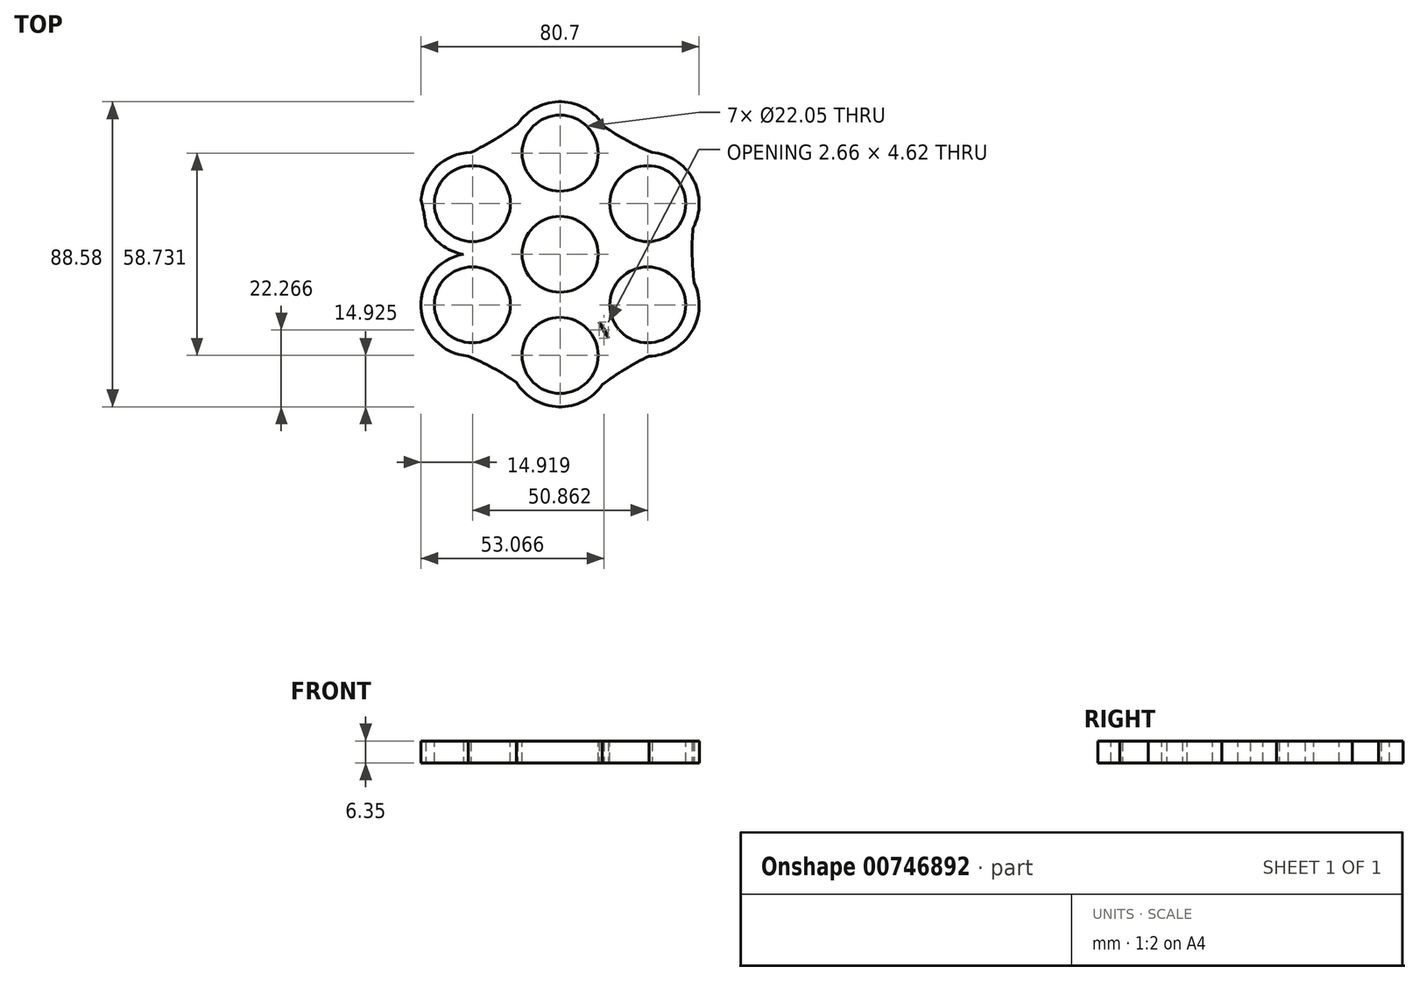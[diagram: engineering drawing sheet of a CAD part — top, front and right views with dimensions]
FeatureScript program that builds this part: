
annotation { "Feature Type Name" : "Feature", "Feature Type Description" : "" }
export const myFeature = defineFeature(function(context is Context, id is Id, definition is map)
    precondition{}
    {
        {
            var Q0;
            Q0=qCreatedBy(makeId("Top.planeOp"),FACE);
            var sketch = newSketch(context, id + "F0", { "sketchPlane" : qUnion([Q0])});
            skCircle(sketch, "E0", {"center": v(0, 0) * mm, "radius": 14.92 * mm});
            skCircle(sketch, "E1", {"center": v(0, 29.37) * mm, "radius": 14.92 * mm});
            skCircle(sketch, "E2.1.0", {"center": v(-25.43, 14.68) * mm, "radius": 14.92 * mm});
            skCircle(sketch, "E2.2.0", {"center": v(-25.43, -14.68) * mm, "radius": 14.92 * mm});
            skCircle(sketch, "E2.3.0", {"center": v(0, -29.37) * mm, "radius": 14.92 * mm});
            skCircle(sketch, "E2.4.0", {"center": v(25.43, -14.68) * mm, "radius": 14.92 * mm});
            skCircle(sketch, "E2.5.0", {"center": v(25.43, 14.68) * mm, "radius": 14.92 * mm});
            skArc(sketch, "E3", {"start": v(-35.23, 25.94) * mm, "mid": v(-19.89, 32.73) * mm, "end": v(-6.48, 42.8) * mm});
            skArc(sketch, "E4.1.0", {"start": v(-40.08, -17.54) * mm, "mid": v(-38.29, -0.86) * mm, "end": v(-40.31, 15.8) * mm});
            skArc(sketch, "E4.2.0", {"start": v(-4.84, -43.48) * mm, "mid": v(-18.4, -33.59) * mm, "end": v(-33.84, -27.01) * mm});
            skArc(sketch, "E4.3.0", {"start": v(35.23, -25.94) * mm, "mid": v(19.89, -32.73) * mm, "end": v(6.48, -42.8) * mm});
            skArc(sketch, "E4.4.0", {"start": v(40.08, 17.54) * mm, "mid": v(38.29, 0.86) * mm, "end": v(40.31, -15.8) * mm});
            skArc(sketch, "E4.5.0", {"start": v(4.84, 43.48) * mm, "mid": v(18.4, 33.59) * mm, "end": v(33.84, 27.01) * mm});
            skSolve(sketch);
        }
        {
            var Q0;
            {var subQ1=sQuery(id+"F0.wireOp",EDGE,"E0");var subQ9=sQuery(id+"F0.wireOp",EDGE,"E2.5.0");var subQ14=makeQuery(id+"F0.imprint","INTERSECT",VERTEX,{"disambiguationData":[OD(0.0)],"derivedFrom":[subQ1,subQ9]});Q0=makeQuery(id+"F0.imprint","IMPRINT",FACE,{"disambiguationData":[TD([[makeQuery(id+"F0.imprint","IMPRINT",EDGE,{"disambiguationData":[TD([[subQ14,-1.0]])],"derivedFrom":subQ1}),1.0]])]});}
            var sketch = newSketch(context, id + "F1", { "sketchPlane" : qUnion([Q0])});
            skSolve(sketch);
        }
        {
            var Q0;
            {var subQ1=sQuery(id+"F0.wireOp",EDGE,"E2.5.0");var subQ8=sQuery(id+"F0.wireOp",EDGE,"E0");var subQ9=makeQuery(id+"F0.imprint","INTERSECT",VERTEX,{"disambiguationData":[OD(0.0)],"derivedFrom":[subQ8,subQ1]});Q0=makeQuery(id+"F0.imprint","IMPRINT",FACE,{"disambiguationData":[TD([[makeQuery(id+"F0.imprint","IMPRINT",EDGE,{"disambiguationData":[TD([[subQ9,1.0]])],"derivedFrom":subQ8}),-1.0]])]});}
            var Q1;
            {var subQ0=sQuery(id+"F0.wireOp",EDGE,"E2.1.0");var subQ1=sQuery(id+"F0.wireOp",EDGE,"E0");var subQ2=makeQuery(id+"F0.imprint","INTERSECT",VERTEX,{"disambiguationData":[OD(1.0)],"derivedFrom":[subQ1,subQ0]});Q1=makeQuery(id+"F0.imprint","IMPRINT",FACE,{"disambiguationData":[TD([[makeQuery(id+"F0.imprint","IMPRINT",EDGE,{"disambiguationData":[TD([[subQ2,-1.0]])],"derivedFrom":subQ1}),-1.0]])]});}
            var Q2;
            {var subQ0=sQuery(id+"F0.wireOp",EDGE,"E2.5.0");var subQ1=sQuery(id+"F0.wireOp",EDGE,"E0");var subQ2=makeQuery(id+"F0.imprint","INTERSECT",VERTEX,{"disambiguationData":[OD(1.0)],"derivedFrom":[subQ1,subQ0]});Q2=makeQuery(id+"F0.imprint","IMPRINT",FACE,{"disambiguationData":[TD([[makeQuery(id+"F0.imprint","IMPRINT",EDGE,{"disambiguationData":[TD([[subQ2,1.0]])],"derivedFrom":subQ1}),-1.0]])]});}
            var Q3;
            {var subQ0=sQuery(id+"F0.wireOp",EDGE,"E4.3.0");var subQ1=sQuery(id+"F0.wireOp",EDGE,"E2.3.0");var subQ2=makeQuery(id+"F0.imprint","INTERSECT",VERTEX,{"disambiguationData":[OD(1.0)],"derivedFrom":[subQ1,subQ0]});Q3=makeQuery(id+"F0.imprint","IMPRINT",FACE,{"disambiguationData":[TD([[makeQuery(id+"F0.imprint","IMPRINT",EDGE,{"disambiguationData":[TD([[subQ2,-1.0]])],"derivedFrom":subQ1}),-1.0]])]});}
            var Q4;
            {var subQ0=sQuery(id+"F0.wireOp",EDGE,"E4.1.0");var subQ1=sQuery(id+"F0.wireOp",EDGE,"E2.1.0");var subQ2=makeQuery(id+"F0.imprint","INTERSECT",VERTEX,{"disambiguationData":[OD(1.0)],"derivedFrom":[subQ1,subQ0]});Q4=makeQuery(id+"F0.imprint","IMPRINT",FACE,{"disambiguationData":[TD([[makeQuery(id+"F0.imprint","IMPRINT",EDGE,{"disambiguationData":[TD([[subQ2,-1.0]])],"derivedFrom":subQ1}),-1.0]])]});}
            var Q5;
            {var subQ1=sQuery(id+"F0.wireOp",EDGE,"E2.1.0");var subQ11=sQuery(id+"F0.wireOp",EDGE,"E0");var subQ14=makeQuery(id+"F0.imprint","INTERSECT",VERTEX,{"disambiguationData":[OD(0.0)],"derivedFrom":[subQ11,subQ1]});Q5=makeQuery(id+"F0.imprint","IMPRINT",FACE,{"disambiguationData":[TD([[makeQuery(id+"F0.imprint","IMPRINT",EDGE,{"disambiguationData":[TD([[subQ14,-1.0]])],"derivedFrom":subQ11}),-1.0]])]});}
            var Q6;
            {var subQ1=sQuery(id+"F0.wireOp",EDGE,"E2.2.0");var subQ11=sQuery(id+"F0.wireOp",EDGE,"E0");var subQ14=makeQuery(id+"F0.imprint","INTERSECT",VERTEX,{"disambiguationData":[OD(0.0)],"derivedFrom":[subQ11,subQ1]});Q6=makeQuery(id+"F0.imprint","IMPRINT",FACE,{"disambiguationData":[TD([[makeQuery(id+"F0.imprint","IMPRINT",EDGE,{"disambiguationData":[TD([[subQ14,-1.0]])],"derivedFrom":subQ11}),-1.0]])]});}
            var Q7;
            {var subQ0=sQuery(id+"F0.wireOp",EDGE,"E4.5.0");var subQ1=sQuery(id+"F0.wireOp",EDGE,"E1");var subQ2=makeQuery(id+"F0.imprint","INTERSECT",VERTEX,{"disambiguationData":[OD(1.0)],"derivedFrom":[subQ1,subQ0]});Q7=makeQuery(id+"F0.imprint","IMPRINT",FACE,{"disambiguationData":[TD([[makeQuery(id+"F0.imprint","IMPRINT",EDGE,{"disambiguationData":[TD([[subQ2,1.0]])],"derivedFrom":subQ1}),-1.0]])]});}
            var Q8;
            {var subQ1=sQuery(id+"F0.wireOp",EDGE,"E1");var subQ8=sQuery(id+"F0.wireOp",EDGE,"E0");var subQ9=makeQuery(id+"F0.imprint","INTERSECT",VERTEX,{"disambiguationData":[OD(0.0)],"derivedFrom":[subQ8,subQ1]});Q8=makeQuery(id+"F0.imprint","IMPRINT",FACE,{"disambiguationData":[TD([[makeQuery(id+"F0.imprint","IMPRINT",EDGE,{"disambiguationData":[TD([[subQ9,-1.0]])],"derivedFrom":subQ8}),-1.0]])]});}
            var Q9;
            {var subQ0=sQuery(id+"F0.wireOp",EDGE,"E2.2.0");var subQ1=sQuery(id+"F0.wireOp",EDGE,"E0");var subQ2=makeQuery(id+"F0.imprint","INTERSECT",VERTEX,{"disambiguationData":[OD(1.0)],"derivedFrom":[subQ1,subQ0]});Q9=makeQuery(id+"F0.imprint","IMPRINT",FACE,{"disambiguationData":[TD([[makeQuery(id+"F0.imprint","IMPRINT",EDGE,{"disambiguationData":[TD([[subQ2,-1.0]])],"derivedFrom":subQ1}),-1.0]])]});}
            var Q10;
            {var subQ0=sQuery(id+"F0.wireOp",EDGE,"E4.4.0");var subQ1=sQuery(id+"F0.wireOp",EDGE,"E2.4.0");var subQ2=makeQuery(id+"F0.imprint","INTERSECT",VERTEX,{"disambiguationData":[OD(1.0)],"derivedFrom":[subQ1,subQ0]});Q10=makeQuery(id+"F0.imprint","IMPRINT",FACE,{"disambiguationData":[TD([[makeQuery(id+"F0.imprint","IMPRINT",EDGE,{"disambiguationData":[TD([[subQ2,-1.0]])],"derivedFrom":subQ1}),-1.0]])]});}
            var Q11;
            {var subQ1=sQuery(id+"F0.wireOp",EDGE,"E2.3.0");var subQ11=sQuery(id+"F0.wireOp",EDGE,"E0");var subQ15=makeQuery(id+"F0.imprint","INTERSECT",VERTEX,{"disambiguationData":[OD(0.0)],"derivedFrom":[subQ11,subQ1]});Q11=makeQuery(id+"F0.imprint","IMPRINT",FACE,{"disambiguationData":[TD([[makeQuery(id+"F0.imprint","IMPRINT",EDGE,{"disambiguationData":[TD([[subQ15,-1.0]])],"derivedFrom":subQ11}),-1.0]])]});}
            var Q12;
            {var subQ0=sQuery(id+"F0.wireOp",EDGE,"E4.2.0");var subQ1=sQuery(id+"F0.wireOp",EDGE,"E2.2.0");var subQ2=makeQuery(id+"F0.imprint","INTERSECT",VERTEX,{"disambiguationData":[OD(1.0)],"derivedFrom":[subQ1,subQ0]});Q12=makeQuery(id+"F0.imprint","IMPRINT",FACE,{"disambiguationData":[TD([[makeQuery(id+"F0.imprint","IMPRINT",EDGE,{"disambiguationData":[TD([[subQ2,-1.0]])],"derivedFrom":subQ1}),-1.0]])]});}
            var Q13;
            {var subQ0=sQuery(id+"F0.wireOp",EDGE,"E3");var subQ1=sQuery(id+"F0.wireOp",EDGE,"E1");var subQ2=makeQuery(id+"F0.imprint","INTERSECT",VERTEX,{"disambiguationData":[OD(1.0)],"derivedFrom":[subQ1,subQ0]});Q13=makeQuery(id+"F0.imprint","IMPRINT",FACE,{"disambiguationData":[TD([[makeQuery(id+"F0.imprint","IMPRINT",EDGE,{"disambiguationData":[TD([[subQ2,-1.0]])],"derivedFrom":subQ1}),-1.0]])]});}
            var Q14;
            {var subQ0=sQuery(id+"F0.wireOp",EDGE,"E2.3.0");var subQ1=sQuery(id+"F0.wireOp",EDGE,"E0");var subQ2=makeQuery(id+"F0.imprint","INTERSECT",VERTEX,{"disambiguationData":[OD(1.0)],"derivedFrom":[subQ1,subQ0]});Q14=makeQuery(id+"F0.imprint","IMPRINT",FACE,{"disambiguationData":[TD([[makeQuery(id+"F0.imprint","IMPRINT",EDGE,{"disambiguationData":[TD([[subQ2,-1.0]])],"derivedFrom":subQ1}),-1.0]])]});}
            var Q15;
            {var subQ0=sQuery(id+"F0.wireOp",EDGE,"E1");var subQ1=sQuery(id+"F0.wireOp",EDGE,"E0");var subQ2=makeQuery(id+"F0.imprint","INTERSECT",VERTEX,{"disambiguationData":[OD(1.0)],"derivedFrom":[subQ1,subQ0]});Q15=makeQuery(id+"F0.imprint","IMPRINT",FACE,{"disambiguationData":[TD([[makeQuery(id+"F0.imprint","IMPRINT",EDGE,{"disambiguationData":[TD([[subQ2,-1.0]])],"derivedFrom":subQ1}),-1.0]])]});}
            var Q16;
            {var subQ1=sQuery(id+"F0.wireOp",EDGE,"E2.4.0");var subQ9=sQuery(id+"F0.wireOp",EDGE,"E0");var subQ14=makeQuery(id+"F0.imprint","INTERSECT",VERTEX,{"disambiguationData":[OD(0.0)],"derivedFrom":[subQ9,subQ1]});Q16=makeQuery(id+"F0.imprint","IMPRINT",FACE,{"disambiguationData":[TD([[makeQuery(id+"F0.imprint","IMPRINT",EDGE,{"disambiguationData":[TD([[subQ14,-1.0]])],"derivedFrom":subQ9}),-1.0]])]});}
            var Q17;
            {var subQ1=sQuery(id+"F0.wireOp",EDGE,"E0");var subQ13=sQuery(id+"F0.wireOp",EDGE,"E2.5.0");var subQ18=makeQuery(id+"F0.imprint","INTERSECT",VERTEX,{"disambiguationData":[OD(0.0)],"derivedFrom":[subQ1,subQ13]});Q17=makeQuery(id+"F1.imprint","IMPRINT",FACE,{"disambiguationData":[TD([[makeQuery(id+"F1.imprint","IMPRINT",EDGE,{"derivedFrom":makeQuery(id+"F0.imprint","IMPRINT",EDGE,{"disambiguationData":[TD([[subQ18,-1.0]])],"derivedFrom":subQ1})}),1.0]])]});}
            var Q18;
            {var subQ0=sQuery(id+"F0.wireOp",EDGE,"E2.5.0");var subQ1=sQuery(id+"F0.wireOp",EDGE,"E1");var subQ2=makeQuery(id+"F0.imprint","INTERSECT",VERTEX,{"disambiguationData":[OD(0.0)],"derivedFrom":[subQ1,subQ0]});Q18=makeQuery(id+"F0.imprint","IMPRINT",FACE,{"disambiguationData":[TD([[makeQuery(id+"F0.imprint","IMPRINT",EDGE,{"disambiguationData":[TD([[subQ2,-1.0]])],"derivedFrom":subQ1}),1.0]])]});}
            var Q19;
            {var subQ0=sQuery(id+"F0.wireOp",EDGE,"E2.5.0");var subQ1=sQuery(id+"F0.wireOp",EDGE,"E2.4.0");var subQ2=makeQuery(id+"F0.imprint","INTERSECT",VERTEX,{"disambiguationData":[OD(0.0)],"derivedFrom":[subQ1,subQ0]});Q19=makeQuery(id+"F0.imprint","IMPRINT",FACE,{"disambiguationData":[TD([[makeQuery(id+"F0.imprint","IMPRINT",EDGE,{"disambiguationData":[TD([[subQ2,-1.0]])],"derivedFrom":subQ1}),1.0]])]});}
            var Q20;
            {var subQ0=sQuery(id+"F0.wireOp",EDGE,"E1");var subQ1=sQuery(id+"F0.wireOp",EDGE,"E0");var subQ2=makeQuery(id+"F0.imprint","INTERSECT",VERTEX,{"disambiguationData":[OD(0.0)],"derivedFrom":[subQ1,subQ0]});Q20=makeQuery(id+"F0.imprint","IMPRINT",FACE,{"disambiguationData":[TD([[makeQuery(id+"F0.imprint","IMPRINT",EDGE,{"disambiguationData":[TD([[subQ2,-1.0]])],"derivedFrom":subQ1}),1.0]])]});}
            var Q21;
            {var subQ0=sQuery(id+"F0.wireOp",EDGE,"E4.5.0");var subQ1=sQuery(id+"F0.wireOp",EDGE,"E1");var subQ2=makeQuery(id+"F0.imprint","INTERSECT",VERTEX,{"disambiguationData":[OD(0.0)],"derivedFrom":[subQ1,subQ0]});Q21=makeQuery(id+"F0.imprint","IMPRINT",FACE,{"disambiguationData":[TD([[makeQuery(id+"F0.imprint","IMPRINT",EDGE,{"disambiguationData":[TD([[subQ2,1.0]])],"derivedFrom":subQ1}),1.0]])]});}
            var Q22;
            {var subQ0=sQuery(id+"F0.wireOp",EDGE,"E3");var subQ1=sQuery(id+"F0.wireOp",EDGE,"E1");var subQ2=makeQuery(id+"F0.imprint","INTERSECT",VERTEX,{"disambiguationData":[OD(0.0)],"derivedFrom":[subQ1,subQ0]});Q22=makeQuery(id+"F0.imprint","IMPRINT",FACE,{"disambiguationData":[TD([[makeQuery(id+"F0.imprint","IMPRINT",EDGE,{"disambiguationData":[TD([[subQ2,-1.0]])],"derivedFrom":subQ1}),1.0]])]});}
            var Q23;
            {var subQ0=sQuery(id+"F0.wireOp",EDGE,"E3");var subQ1=sQuery(id+"F0.wireOp",EDGE,"E2.1.0");var subQ2=makeQuery(id+"F0.imprint","INTERSECT",VERTEX,{"disambiguationData":[OD(0.0)],"derivedFrom":[subQ1,subQ0]});Q23=makeQuery(id+"F0.imprint","IMPRINT",FACE,{"disambiguationData":[TD([[makeQuery(id+"F0.imprint","IMPRINT",EDGE,{"disambiguationData":[TD([[subQ2,1.0]])],"derivedFrom":subQ1}),1.0]])]});}
            var Q24;
            {var subQ0=sQuery(id+"F0.wireOp",EDGE,"E4.1.0");var subQ1=sQuery(id+"F0.wireOp",EDGE,"E2.1.0");var subQ2=makeQuery(id+"F0.imprint","INTERSECT",VERTEX,{"disambiguationData":[OD(0.0)],"derivedFrom":[subQ1,subQ0]});Q24=makeQuery(id+"F0.imprint","IMPRINT",FACE,{"disambiguationData":[TD([[makeQuery(id+"F0.imprint","IMPRINT",EDGE,{"disambiguationData":[TD([[subQ2,-1.0]])],"derivedFrom":subQ1}),1.0]])]});}
            var Q25;
            {var subQ1=sQuery(id+"F0.wireOp",EDGE,"E0");var subQ9=sQuery(id+"F0.wireOp",EDGE,"E2.5.0");var subQ14=makeQuery(id+"F0.imprint","INTERSECT",VERTEX,{"disambiguationData":[OD(0.0)],"derivedFrom":[subQ1,subQ9]});Q25=makeQuery(id+"F0.imprint","IMPRINT",FACE,{"disambiguationData":[TD([[makeQuery(id+"F0.imprint","IMPRINT",EDGE,{"disambiguationData":[TD([[subQ14,-1.0]])],"derivedFrom":subQ1}),1.0]])]});}
            var Q26;
            {var subQ0=sQuery(id+"F0.wireOp",EDGE,"E2.1.0");var subQ1=sQuery(id+"F0.wireOp",EDGE,"E1");var subQ2=makeQuery(id+"F0.imprint","INTERSECT",VERTEX,{"disambiguationData":[OD(0.0)],"derivedFrom":[subQ1,subQ0]});Q26=makeQuery(id+"F0.imprint","IMPRINT",FACE,{"disambiguationData":[TD([[makeQuery(id+"F0.imprint","IMPRINT",EDGE,{"disambiguationData":[TD([[subQ2,-1.0]])],"derivedFrom":subQ1}),1.0]])]});}
            var Q27;
            {var subQ0=sQuery(id+"F0.wireOp",EDGE,"E4.1.0");var subQ1=sQuery(id+"F0.wireOp",EDGE,"E2.2.0");var subQ2=makeQuery(id+"F0.imprint","INTERSECT",VERTEX,{"disambiguationData":[OD(0.0)],"derivedFrom":[subQ1,subQ0]});Q27=makeQuery(id+"F0.imprint","IMPRINT",FACE,{"disambiguationData":[TD([[makeQuery(id+"F0.imprint","IMPRINT",EDGE,{"disambiguationData":[TD([[subQ2,1.0]])],"derivedFrom":subQ1}),1.0]])]});}
            var Q28;
            {var subQ0=sQuery(id+"F0.wireOp",EDGE,"E4.2.0");var subQ1=sQuery(id+"F0.wireOp",EDGE,"E2.2.0");var subQ2=makeQuery(id+"F0.imprint","INTERSECT",VERTEX,{"disambiguationData":[OD(0.0)],"derivedFrom":[subQ1,subQ0]});Q28=makeQuery(id+"F0.imprint","IMPRINT",FACE,{"disambiguationData":[TD([[makeQuery(id+"F0.imprint","IMPRINT",EDGE,{"disambiguationData":[TD([[subQ2,-1.0]])],"derivedFrom":subQ1}),1.0]])]});}
            var Q29;
            {var subQ0=sQuery(id+"F0.wireOp",EDGE,"E4.2.0");var subQ1=sQuery(id+"F0.wireOp",EDGE,"E2.3.0");var subQ2=makeQuery(id+"F0.imprint","INTERSECT",VERTEX,{"disambiguationData":[OD(0.0)],"derivedFrom":[subQ1,subQ0]});Q29=makeQuery(id+"F0.imprint","IMPRINT",FACE,{"disambiguationData":[TD([[makeQuery(id+"F0.imprint","IMPRINT",EDGE,{"disambiguationData":[TD([[subQ2,1.0]])],"derivedFrom":subQ1}),1.0]])]});}
            var Q30;
            {var subQ0=sQuery(id+"F0.wireOp",EDGE,"E4.3.0");var subQ1=sQuery(id+"F0.wireOp",EDGE,"E2.3.0");var subQ2=makeQuery(id+"F0.imprint","INTERSECT",VERTEX,{"disambiguationData":[OD(0.0)],"derivedFrom":[subQ1,subQ0]});Q30=makeQuery(id+"F0.imprint","IMPRINT",FACE,{"disambiguationData":[TD([[makeQuery(id+"F0.imprint","IMPRINT",EDGE,{"disambiguationData":[TD([[subQ2,-1.0]])],"derivedFrom":subQ1}),1.0]])]});}
            var Q31;
            {var subQ0=sQuery(id+"F0.wireOp",EDGE,"E4.3.0");var subQ1=sQuery(id+"F0.wireOp",EDGE,"E2.4.0");var subQ2=makeQuery(id+"F0.imprint","INTERSECT",VERTEX,{"disambiguationData":[OD(0.0)],"derivedFrom":[subQ1,subQ0]});Q31=makeQuery(id+"F0.imprint","IMPRINT",FACE,{"disambiguationData":[TD([[makeQuery(id+"F0.imprint","IMPRINT",EDGE,{"disambiguationData":[TD([[subQ2,1.0]])],"derivedFrom":subQ1}),1.0]])]});}
            var Q32;
            {var subQ0=sQuery(id+"F0.wireOp",EDGE,"E4.4.0");var subQ1=sQuery(id+"F0.wireOp",EDGE,"E2.4.0");var subQ2=makeQuery(id+"F0.imprint","INTERSECT",VERTEX,{"disambiguationData":[OD(0.0)],"derivedFrom":[subQ1,subQ0]});Q32=makeQuery(id+"F0.imprint","IMPRINT",FACE,{"disambiguationData":[TD([[makeQuery(id+"F0.imprint","IMPRINT",EDGE,{"disambiguationData":[TD([[subQ2,-1.0]])],"derivedFrom":subQ1}),1.0]])]});}
            var Q33;
            {var subQ0=sQuery(id+"F0.wireOp",EDGE,"E4.4.0");var subQ1=sQuery(id+"F0.wireOp",EDGE,"E2.5.0");var subQ2=makeQuery(id+"F0.imprint","INTERSECT",VERTEX,{"disambiguationData":[OD(0.0)],"derivedFrom":[subQ1,subQ0]});Q33=makeQuery(id+"F0.imprint","IMPRINT",FACE,{"disambiguationData":[TD([[makeQuery(id+"F0.imprint","IMPRINT",EDGE,{"disambiguationData":[TD([[subQ2,1.0]])],"derivedFrom":subQ1}),1.0]])]});}
            var Q34;
            {var subQ0=sQuery(id+"F0.wireOp",EDGE,"E4.5.0");var subQ1=sQuery(id+"F0.wireOp",EDGE,"E2.5.0");var subQ2=makeQuery(id+"F0.imprint","INTERSECT",VERTEX,{"disambiguationData":[OD(0.0)],"derivedFrom":[subQ1,subQ0]});Q34=makeQuery(id+"F0.imprint","IMPRINT",FACE,{"disambiguationData":[TD([[makeQuery(id+"F0.imprint","IMPRINT",EDGE,{"disambiguationData":[TD([[subQ2,-1.0]])],"derivedFrom":subQ1}),1.0]])]});}
            var Q35;
            {var subQ0=sQuery(id+"F0.wireOp",EDGE,"E2.5.0");var subQ1=sQuery(id+"F0.wireOp",EDGE,"E0");var subQ2=makeQuery(id+"F0.imprint","INTERSECT",VERTEX,{"disambiguationData":[OD(0.0)],"derivedFrom":[subQ1,subQ0]});Q35=makeQuery(id+"F0.imprint","IMPRINT",FACE,{"disambiguationData":[TD([[makeQuery(id+"F0.imprint","IMPRINT",EDGE,{"disambiguationData":[TD([[subQ2,1.0]])],"derivedFrom":subQ1}),1.0]])]});}
            var Q36;
            {var subQ0=sQuery(id+"F0.wireOp",EDGE,"E2.4.0");var subQ1=sQuery(id+"F0.wireOp",EDGE,"E2.3.0");var subQ2=makeQuery(id+"F0.imprint","INTERSECT",VERTEX,{"disambiguationData":[OD(0.0)],"derivedFrom":[subQ1,subQ0]});Q36=makeQuery(id+"F0.imprint","IMPRINT",FACE,{"disambiguationData":[TD([[makeQuery(id+"F0.imprint","IMPRINT",EDGE,{"disambiguationData":[TD([[subQ2,-1.0]])],"derivedFrom":subQ1}),1.0]])]});}
            var Q37;
            {var subQ0=sQuery(id+"F0.wireOp",EDGE,"E2.2.0");var subQ1=sQuery(id+"F0.wireOp",EDGE,"E2.1.0");var subQ2=makeQuery(id+"F0.imprint","INTERSECT",VERTEX,{"disambiguationData":[OD(0.0)],"derivedFrom":[subQ1,subQ0]});Q37=makeQuery(id+"F0.imprint","IMPRINT",FACE,{"disambiguationData":[TD([[makeQuery(id+"F0.imprint","IMPRINT",EDGE,{"disambiguationData":[TD([[subQ2,-1.0]])],"derivedFrom":subQ1}),1.0]])]});}
            var Q38;
            {var subQ0=sQuery(id+"F0.wireOp",EDGE,"E2.5.0");var subQ1=sQuery(id+"F0.wireOp",EDGE,"E0");var subQ2=makeQuery(id+"F0.imprint","INTERSECT",VERTEX,{"disambiguationData":[OD(0.0)],"derivedFrom":[subQ1,subQ0]});Q38=makeQuery(id+"F0.imprint","IMPRINT",FACE,{"disambiguationData":[TD([[makeQuery(id+"F0.imprint","IMPRINT",EDGE,{"disambiguationData":[TD([[subQ2,-1.0]])],"derivedFrom":subQ1}),-1.0]])]});}
            var Q39;
            {var subQ0=sQuery(id+"F0.wireOp",EDGE,"E2.4.0");var subQ1=sQuery(id+"F0.wireOp",EDGE,"E0");var subQ2=makeQuery(id+"F0.imprint","INTERSECT",VERTEX,{"disambiguationData":[OD(0.0)],"derivedFrom":[subQ1,subQ0]});Q39=makeQuery(id+"F0.imprint","IMPRINT",FACE,{"disambiguationData":[TD([[makeQuery(id+"F0.imprint","IMPRINT",EDGE,{"disambiguationData":[TD([[subQ2,-1.0]])],"derivedFrom":subQ1}),1.0]])]});}
            var Q40;
            {var subQ0=sQuery(id+"F0.wireOp",EDGE,"E2.3.0");var subQ1=sQuery(id+"F0.wireOp",EDGE,"E2.2.0");var subQ2=makeQuery(id+"F0.imprint","INTERSECT",VERTEX,{"disambiguationData":[OD(0.0)],"derivedFrom":[subQ1,subQ0]});Q40=makeQuery(id+"F0.imprint","IMPRINT",FACE,{"disambiguationData":[TD([[makeQuery(id+"F0.imprint","IMPRINT",EDGE,{"disambiguationData":[TD([[subQ2,-1.0]])],"derivedFrom":subQ1}),1.0]])]});}
            var Q41;
            {var subQ0=sQuery(id+"F0.wireOp",EDGE,"E2.2.0");var subQ1=sQuery(id+"F0.wireOp",EDGE,"E0");var subQ2=makeQuery(id+"F0.imprint","INTERSECT",VERTEX,{"disambiguationData":[OD(0.0)],"derivedFrom":[subQ1,subQ0]});Q41=makeQuery(id+"F0.imprint","IMPRINT",FACE,{"disambiguationData":[TD([[makeQuery(id+"F0.imprint","IMPRINT",EDGE,{"disambiguationData":[TD([[subQ2,-1.0]])],"derivedFrom":subQ1}),1.0]])]});}
            var Q42;
            {var subQ0=sQuery(id+"F0.wireOp",EDGE,"E2.1.0");var subQ1=sQuery(id+"F0.wireOp",EDGE,"E0");var subQ2=makeQuery(id+"F0.imprint","INTERSECT",VERTEX,{"disambiguationData":[OD(0.0)],"derivedFrom":[subQ1,subQ0]});Q42=makeQuery(id+"F0.imprint","IMPRINT",FACE,{"disambiguationData":[TD([[makeQuery(id+"F0.imprint","IMPRINT",EDGE,{"disambiguationData":[TD([[subQ2,-1.0]])],"derivedFrom":subQ1}),1.0]])]});}
            var Q43;
            {var subQ0=sQuery(id+"F0.wireOp",EDGE,"E2.3.0");var subQ1=sQuery(id+"F0.wireOp",EDGE,"E0");var subQ2=makeQuery(id+"F0.imprint","INTERSECT",VERTEX,{"disambiguationData":[OD(0.0)],"derivedFrom":[subQ1,subQ0]});Q43=makeQuery(id+"F0.imprint","IMPRINT",FACE,{"disambiguationData":[TD([[makeQuery(id+"F0.imprint","IMPRINT",EDGE,{"disambiguationData":[TD([[subQ2,-1.0]])],"derivedFrom":subQ1}),1.0]])]});}
            extrude(context, id + "F2", {"entities" : qUnion([Q0, Q1, Q2, Q3, Q4, Q5, Q6, Q7, Q8, Q9, Q10, Q11, Q12, Q13, Q14, Q15, Q16, Q17, Q18, Q19, Q20, Q21, Q22, Q23, Q24, Q25, Q26, Q27, Q28, Q29, Q30, Q31, Q32, Q33, Q34, Q35, Q36, Q37, Q38, Q39, Q40, Q41, Q42, Q43]), "depth" : 6.35 * mm, "offsetDistance" : 25.4 * mm});
        }
        {
            var Q0;
            Q0=makeQuery(id+"F2.opExtrude","CAP_FACE",FACE,{"disambiguationData":[OSD([sQuery(id+"F0.wireOp",EDGE,"E1"),sQuery(id+"F0.wireOp",EDGE,"E2.1.0"),sQuery(id+"F0.wireOp",EDGE,"E2.2.0"),sQuery(id+"F0.wireOp",EDGE,"E2.3.0"),sQuery(id+"F0.wireOp",EDGE,"E2.4.0"),sQuery(id+"F0.wireOp",EDGE,"E2.5.0"),sQuery(id+"F0.wireOp",EDGE,"E3"),sQuery(id+"F0.wireOp",EDGE,"E4.1.0"),sQuery(id+"F0.wireOp",EDGE,"E4.2.0"),sQuery(id+"F0.wireOp",EDGE,"E4.3.0"),sQuery(id+"F0.wireOp",EDGE,"E4.4.0"),sQuery(id+"F0.wireOp",EDGE,"E4.5.0")])],"isStart":false});
            var sketch = newSketch(context, id + "F3", { "sketchPlane" : qUnion([Q0])});
            skCircle(sketch, "E5", {"center": v(0, 0) * mm, "radius": 11.02 * mm});
            skCircle(sketch, "E6", {"center": v(25.43, 14.68) * mm, "radius": 11.02 * mm});
            skCircle(sketch, "E7", {"center": v(25.43, -14.68) * mm, "radius": 11.02 * mm});
            skCircle(sketch, "E8", {"center": v(0, -29.37) * mm, "radius": 11.02 * mm});
            skCircle(sketch, "E9", {"center": v(-25.43, -14.68) * mm, "radius": 11.02 * mm});
            skCircle(sketch, "E10", {"center": v(-25.43, 14.68) * mm, "radius": 11.02 * mm});
            skCircle(sketch, "E11", {"center": v(0, 29.37) * mm, "radius": 11.02 * mm});
            skSolve(sketch);
        }
        {
            var Q0;
            Q0 = qSketchRegion(id + "F3", true);
            extrude(context, id + "F4", {"entities" : qUnion([Q0]), "operationType" : NewBodyOperationType.REMOVE, "oppositeDirection" : true, "depth" : 6.35 * mm, "offsetDistance" : 25.4 * mm});
        }
    });
